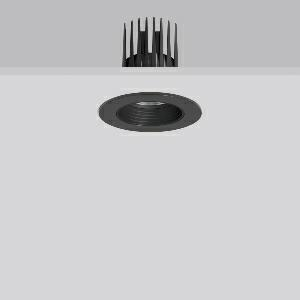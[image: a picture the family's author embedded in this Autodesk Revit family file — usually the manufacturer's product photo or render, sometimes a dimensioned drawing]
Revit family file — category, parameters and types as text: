
# Revit family: heledon_mini_e_901754_003_1_21dd
name_source: partatom
category: Lighting Fixtures
units: mm (PartAtom-declared; Revit-internal decimal feet)

## family parameters
Cut with Voids When Loaded = No
Host = Face
Light Source = No
Part Type = Normal
Room Calculation Point = No
Round Connector Dimension = Use Diameter
Shared = No

## types (1)
- HELEDON mini E (1 x LED Modul 940, 3500 lm, 4000)
    Apparent Load = 29 VA
    Approval mark = CE
    CIE Flux Codes = 80 99 100 100 100
    Color Rendering = 92
    Color Temperature = 4000
    Default Elevation = 1800 mm
    Description = Series: HELEDON mini
Round recessed downlight. Housing: die-cast aluminium, powder-coated. Black plastic ring and recessed LED to prevent glare from the side. Optical assembly with lens made of plastic (polycarbonate) for the best homogeneous light distribution - can be changed without tools. Best colour rendering index Ra>90. Suitable for Recessed ceiling mounting. Installation without tools thanks to spring fastening system. Including separate LED converter with connecting cable 600 mm.High quality converter without flickering and stroboscopic effect. Through-wiring box (5 pole) available as accessory. The following accessories can be mounted without use of tools: interchangeable lenses, decorative glasses, honeycomb louvre, clear and frosted diffusers, white interchangeable plastic ring. 
Colour: deep black, matt (RAL 9005)
Diameter: 124 mm
Height: 3 mm
Cut-out diameter: 114 mm
Recess height: 170 mm
Luminaire: recess height: 120 mm
Lamp: LED
Socket: without socket
Colour temperature: 4000K
Colour rendering index (CRI): 92
System power: 29 W
Rated luminous flux: 3500 lm
Luminous efficiency: 121 lm/W
Control gear: Regulated power supply
Protection class: II
Type of protection: IP 20
    Height = 0 mm  [stored 0 ft]
    Lamp = 1 x LED Modul 940
    Lamp Light Flux = 3500 lm
    Lamp count = 1
    Length = 124 mm  [stored 0.406824 ft]
    Lifetime = 50000 h
    Luminous efficacy = 121 lm/W
    Manufacturer = RZB
    ModVariant = No
    Model = 901754.003.1
    Mounting Place = Ceiling
    Mounting Type = Recessed
    Number of Poles = 1
    OnlyDefault = Yes
    Power Factor = 1
    Product Name = HELEDON mini E
    Product group = Recessed downlights
    ProductGroupID = 402
    Protection Class = Protection class II
    Protection Degree = IP 20
    RLX_Detail_Level = 1
    RLX_Emergency_Light_Flux = 0 lm
    RLX_Emergency_Type = 0
    RLX_Emergency_Type_DB = No
    RlxData = <blob elided: 125721 chars, md5=21cad676>
    Socket = socket
    Standby Power = 0 W
    System Light Flux = 3500 lm
    System Power = 29 W
    Type Comments = Product without accessories
    Type Image = 901656.003.jpg
    URL = http://relux.com
    VarID = ---
    Voltage = 230 V
    Voltage Range = 220-240 V
    Weight = 0.00 kg
    Width = 0 mm  [stored 0 ft]

note: [stored X ft] marks values corroborated as IEEE doubles in the binary element streams (Revit-internal decimal feet)

## geometry (parser evidence)
native form markers: Blend x4, Sweep x13
no freeform markers — native parametric forms only
